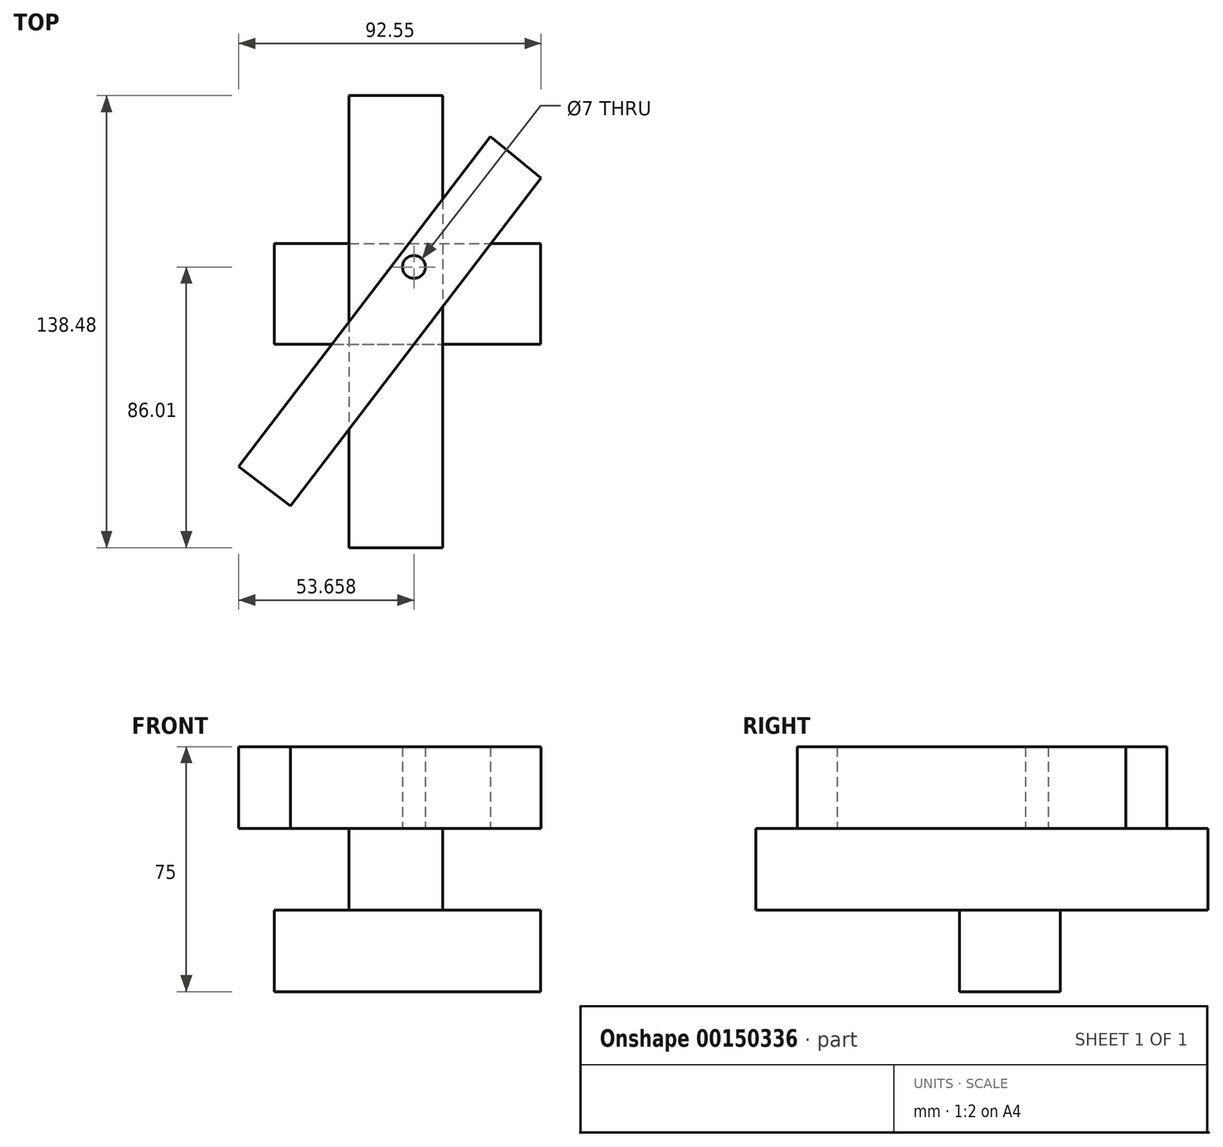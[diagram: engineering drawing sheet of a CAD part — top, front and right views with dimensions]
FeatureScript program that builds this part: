
annotation { "Feature Type Name" : "Feature", "Feature Type Description" : "" }
export const myFeature = defineFeature(function(context is Context, id is Id, definition is map)
    precondition{}
    {
        {
            var Q0;
            Q0=qCreatedBy(makeId("Top.planeOp"),FACE);
            var sketch = newSketch(context, id + "F0", { "sketchPlane" : qUnion([Q0])});
            skLineSegment(sketch, "E0.bottom", {"start": v(-33.98, 14.33) * mm, "end": v(47.63, 14.33) * mm});
            skLineSegment(sketch, "E0.top", {"start": v(-33.98, -16.52) * mm, "end": v(47.63, -16.52) * mm});
            skLineSegment(sketch, "E0.left", {"start": v(-33.98, 14.33) * mm, "end": v(-33.98, -16.52) * mm});
            skLineSegment(sketch, "E0.right", {"start": v(47.63, 14.33) * mm, "end": v(47.63, -16.52) * mm});
            skSolve(sketch);
        }
        {
            var Q0;
            Q0 = qSketchRegion(id + "F0", true);
            var Q1;
            Q1=makeQuery(id+"F0.imprint","IMPRINT",FACE,{"disambiguationData":[TD([[makeQuery(id+"F0.imprint","IMPRINT",EDGE,{"derivedFrom":sQuery(id+"F0.wireOp",EDGE,"E0.bottom")}),-1.0]])]});
            extrude(context, id + "F1", {"entities" : qUnion([Q0, Q1]), "depth" : 25 * mm});
        }
        {
            var Q0;
            Q0=makeQuery(id+"F1.opExtrude","CAP_FACE",FACE,{"disambiguationData":[OSD([sQuery(id+"F0.wireOp",EDGE,"E0.bottom"),sQuery(id+"F0.wireOp",EDGE,"E0.top"),sQuery(id+"F0.wireOp",EDGE,"E0.left"),sQuery(id+"F0.wireOp",EDGE,"E0.right")])],"isStart":false});
            var sketch = newSketch(context, id + "F2", { "sketchPlane" : qUnion([Q0])});
            skLineSegment(sketch, "E1.bottom", {"start": v(-11.06, 59.65) * mm, "end": v(17.6, 59.65) * mm});
            skLineSegment(sketch, "E1.top", {"start": v(-11.06, -78.83) * mm, "end": v(17.6, -78.83) * mm});
            skLineSegment(sketch, "E1.left", {"start": v(-11.06, 59.65) * mm, "end": v(-11.06, -78.83) * mm});
            skLineSegment(sketch, "E1.right", {"start": v(17.6, 59.65) * mm, "end": v(17.6, -78.83) * mm});
            skSolve(sketch);
        }
        {
            var Q0;
            Q0 = qSketchRegion(id + "F2", true);
            var Q1;
            {var subQ0=sQuery(id+"F2.wireOp",EDGE,"E1.bottom");Q1=makeQuery(id+"F2.imprint","IMPRINT",FACE,{"disambiguationData":[TD([[makeQuery(id+"F2.imprint","IMPRINT",EDGE,{"derivedFrom":subQ0}),-1.0]])]});}
            extrude(context, id + "F3", {"entities" : qUnion([Q0, Q1]), "depth" : 25 * mm});
        }
        {
            var Q0;
            Q0=makeQuery(id+"F3.opExtrude","CAP_FACE",FACE,{"disambiguationData":[OSD([sQuery(id+"F2.wireOp",EDGE,"E1.bottom"),sQuery(id+"F2.wireOp",EDGE,"E1.top"),sQuery(id+"F2.wireOp",EDGE,"E1.left"),sQuery(id+"F2.wireOp",EDGE,"E1.right")])],"isStart":false});
            var sketch = newSketch(context, id + "F4", { "sketchPlane" : qUnion([Q0])});
            skLineSegment(sketch, "E2", {"start": v(32.22, 47.09) * mm, "end": v(-44.84, -53.98) * mm});
            skLineSegment(sketch, "E3", {"start": v(-44.84, -53.98) * mm, "end": v(-28.95, -66.1) * mm});
            skLineSegment(sketch, "E4", {"start": v(-28.95, -66.1) * mm, "end": v(47.7, 34.43) * mm});
            skLineSegment(sketch, "E5", {"start": v(47.7, 34.43) * mm, "end": v(32.22, 47.09) * mm});
            skPoint(sketch, "E6", {"position": v(6.3, -2.34) * mm});
            skSolve(sketch);
        }
        {
            var Q0;
            Q0 = qSketchRegion(id + "F4", true);
            var Q1;
            {var subQ0=sQuery(id+"F4.wireOp",EDGE,"Fb4xla2M-f2uC-8B63-TZ92-riwH2eyXFt3v");var subQ1=makeQuery(id+"F3.opExtrude","CAP_EDGE",EDGE,{"disambiguationData":[OSD([sQuery(id+"F2.wireOp",EDGE,"E1.left")])],"isStart":false});var subQ2=makeQuery(id+"F4.imprint","INTERSECT",VERTEX,{"derivedFrom":[subQ1,subQ0]});Q1=makeQuery(id+"F4.imprint","IMPRINT",FACE,{"disambiguationData":[TD([[makeQuery(id+"F4.imprint","IMPRINT",EDGE,{"disambiguationData":[TD([[subQ2,-1.0]])],"derivedFrom":subQ0}),-1.0]])]});}
            extrude(context, id + "F5", {"entities" : qUnion([Q0, Q1]), "depth" : 25 * mm});
        }
        {
            var Q0;
            Q0=makeQuery(id+"F5.opExtrude","CAP_FACE",FACE,{"disambiguationData":[OSD([sQuery(id+"F4.wireOp",EDGE,"E2"),sQuery(id+"F4.wireOp",EDGE,"E3"),sQuery(id+"F4.wireOp",EDGE,"E4"),sQuery(id+"F4.wireOp",EDGE,"E5")])],"isStart":false});
            var sketch = newSketch(context, id + "F6", { "sketchPlane" : qUnion([Q0])});
            skPoint(sketch, "E7", {"position": v(8.82, 7.18) * mm});
            skSolve(sketch);
        }
        {
            var Q0;
            Q0=sQuery(id+"F6.wireOp",VERTEX,"E7");
            var Q1;
            Q1=makeQuery(id+"F5.opExtrude","SWEPT_BODY",BODY,{"disambiguationData":[OSD([sQuery(id+"F4.wireOp",EDGE,"E2"),sQuery(id+"F4.wireOp",EDGE,"E3"),sQuery(id+"F4.wireOp",EDGE,"E4"),sQuery(id+"F4.wireOp",EDGE,"E5")])]});
            hole(context, id + "F7", {"style" : HoleStyle.SIMPLE, "endStyle" : HoleEndStyle.THROUGH, "holeDiameter" : 7 * mm, "locations" : qUnion([Q0]), "scope" : qUnion([Q1]), "isTappedThrough" : true, "startStyle" : HoleStartStyle.PART});
        }
    });
